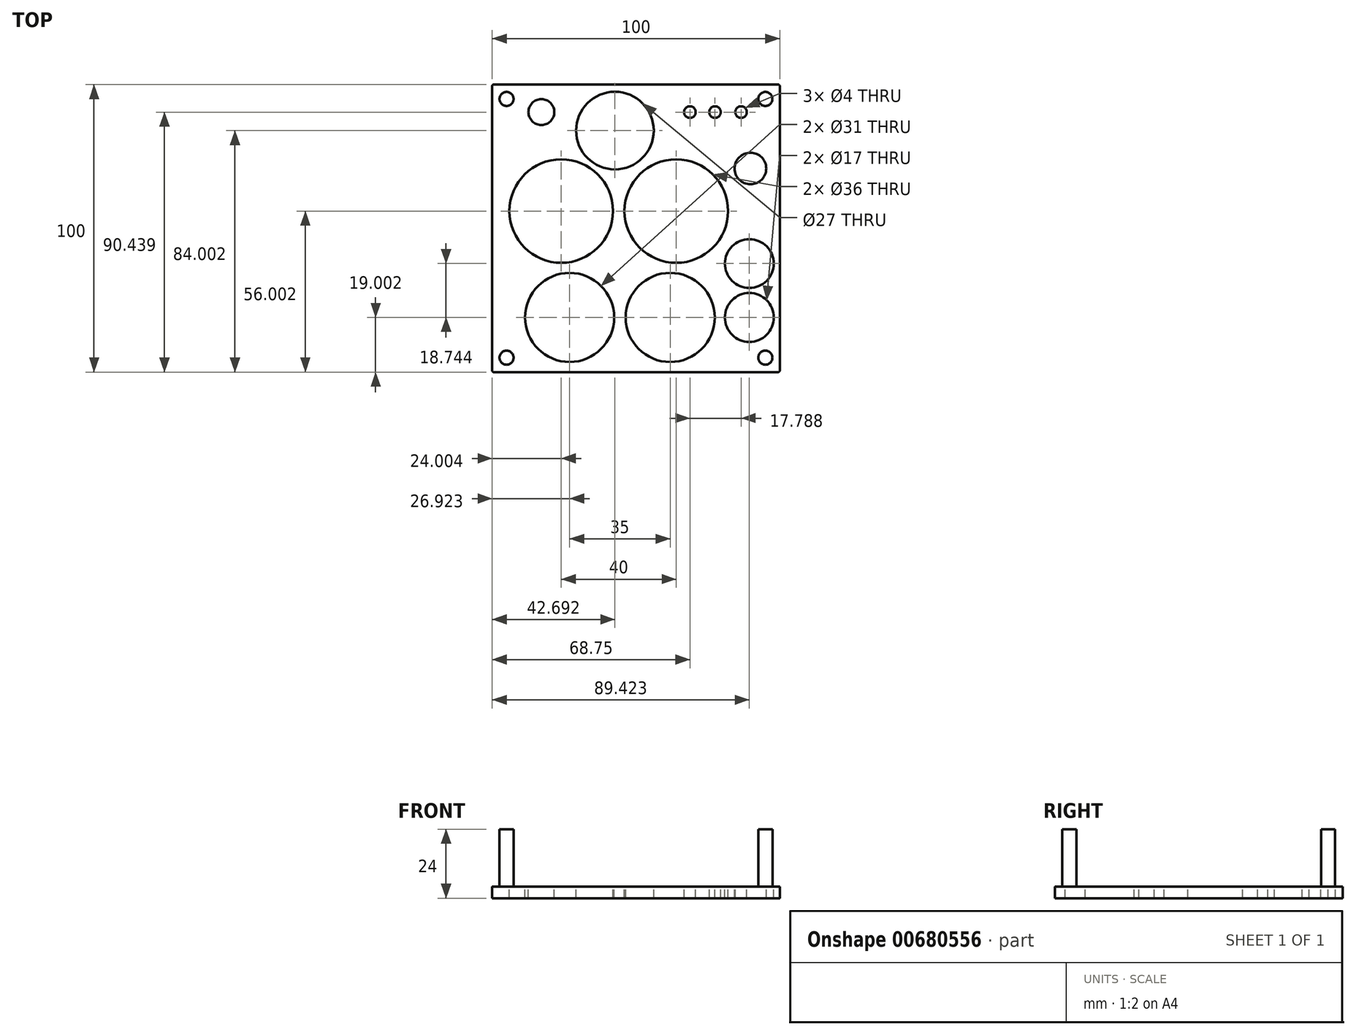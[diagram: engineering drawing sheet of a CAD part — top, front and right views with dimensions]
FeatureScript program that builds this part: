
annotation { "Feature Type Name" : "Feature", "Feature Type Description" : "" }
export const myFeature = defineFeature(function(context is Context, id is Id, definition is map)
    precondition{}
    {
        {
            var Q0;
            Q0=qCreatedBy(makeId("Top.planeOp"),FACE);
            var sketch = newSketch(context, id + "F0", { "sketchPlane" : qUnion([Q0])});
            skLineSegment(sketch, "E0.bottom", {"start": v(-68.75, 48.6) * mm, "end": v(31.25, 48.6) * mm});
            skLineSegment(sketch, "E0.top", {"start": v(-68.75, -51.4) * mm, "end": v(31.25, -51.4) * mm});
            skLineSegment(sketch, "E0.left", {"start": v(-68.75, 48.6) * mm, "end": v(-68.75, -51.4) * mm});
            skLineSegment(sketch, "E0.right", {"start": v(31.25, 48.6) * mm, "end": v(31.25, -51.4) * mm});
            skSolve(sketch);
        }
        {
            var Q0;
            Q0=makeQuery(id+"F0.imprint","IMPRINT",FACE,{"disambiguationData":[TD([[makeQuery(id+"F0.imprint","IMPRINT",EDGE,{"derivedFrom":sQuery(id+"F0.wireOp",EDGE,"E0.bottom")}),-1.0]])]});
            extrude(context, id + "F1", {"entities" : qUnion([Q0]), "depth" : 4 * mm, "offsetDistance" : 25 * mm});
        }
        {
            var Q0;
            Q0=makeQuery(id+"F1.opExtrude","SWEPT_EDGE",EDGE,{"disambiguationData":[OSD([sQuery(id+"F0.wireOp",EDGE,"E0.bottom"),sQuery(id+"F0.wireOp",EDGE,"E0.left")])]});
            var Q1;
            Q1=makeQuery(id+"F1.opExtrude","SWEPT_EDGE",EDGE,{"disambiguationData":[OSD([sQuery(id+"F0.wireOp",EDGE,"E0.bottom"),sQuery(id+"F0.wireOp",EDGE,"E0.right")])]});
            var Q2;
            Q2=makeQuery(id+"F1.opExtrude","SWEPT_EDGE",EDGE,{"disambiguationData":[OSD([sQuery(id+"F0.wireOp",EDGE,"E0.top"),sQuery(id+"F0.wireOp",EDGE,"E0.right")])]});
            var Q3;
            Q3=makeQuery(id+"F1.opExtrude","SWEPT_EDGE",EDGE,{"disambiguationData":[OSD([sQuery(id+"F0.wireOp",EDGE,"E0.top"),sQuery(id+"F0.wireOp",EDGE,"E0.left")])]});
            fillet(context, id + "F2", {"entities" : qUnion([Q0, Q1, Q2, Q3]), "radius" : 0.5 * mm, "tangentPropagation" : true, "allowEdgeOverflow" : false});
        }
        {
            var Q0;
            Q0=makeQuery(id+"F1.opExtrude","CAP_FACE",FACE,{"disambiguationData":[OSD([sQuery(id+"F0.wireOp",EDGE,"E0.bottom"),sQuery(id+"F0.wireOp",EDGE,"E0.top"),sQuery(id+"F0.wireOp",EDGE,"E0.left"),sQuery(id+"F0.wireOp",EDGE,"E0.right")])],"isStart":false});
            var sketch = newSketch(context, id + "F3", { "sketchPlane" : qUnion([Q0])});
            skCircle(sketch, "E1", {"center": v(-63.75, 43.6) * mm, "radius": 2.45 * mm});
            skCircle(sketch, "E2", {"center": v(26.25, 43.6) * mm, "radius": 2.45 * mm});
            skCircle(sketch, "E3", {"center": v(-63.75, -46.4) * mm, "radius": 2.45 * mm});
            skCircle(sketch, "E4", {"center": v(26.25, -46.4) * mm, "radius": 2.45 * mm});
            skSolve(sketch);
        }
        {
            var Q0;
            Q0 = qSketchRegion(id + "F3", true);
            extrude(context, id + "F4", {"entities" : qUnion([Q0]), "operationType" : NewBodyOperationType.ADD, "depth" : 20 * mm, "offsetDistance" : 25 * mm});
        }
        {
            var Q0;
            Q0=makeQuery(id+"F1.opExtrude","CAP_FACE",FACE,{"disambiguationData":[OSD([sQuery(id+"F0.wireOp",EDGE,"E0.bottom"),sQuery(id+"F0.wireOp",EDGE,"E0.top"),sQuery(id+"F0.wireOp",EDGE,"E0.left"),sQuery(id+"F0.wireOp",EDGE,"E0.right")])],"isStart":false});
            var sketch = newSketch(context, id + "F5", { "sketchPlane" : qUnion([Q0])});
            skCircle(sketch, "E5", {"center": v(-44.75, 4.6) * mm, "radius": 18 * mm});
            skCircle(sketch, "E6", {"center": v(-4.75, 4.6) * mm, "radius": 18 * mm});
            skCircle(sketch, "E7", {"center": v(-41.83, -32.4) * mm, "radius": 15.5 * mm});
            skCircle(sketch, "E8", {"center": v(-6.83, -32.4) * mm, "radius": 15.5 * mm});
            skCircle(sketch, "E9", {"center": v(-26.06, 32.6) * mm, "radius": 13.5 * mm});
            skCircle(sketch, "E10", {"center": v(20.67, -32.4) * mm, "radius": 8.5 * mm});
            skCircle(sketch, "E11", {"center": v(20.67, -13.65) * mm, "radius": 8.5 * mm});
            skCircle(sketch, "E12", {"center": v(21.06, 19.42) * mm, "radius": 5.5 * mm});
            skCircle(sketch, "E13", {"center": v(-51.63, 39.04) * mm, "radius": 4.5 * mm});
            skCircle(sketch, "E14", {"center": v(0, 39.04) * mm, "radius": 2 * mm});
            skCircle(sketch, "E15", {"center": v(8.75, 39.04) * mm, "radius": 2 * mm});
            skCircle(sketch, "E16", {"center": v(17.79, 39.04) * mm, "radius": 2 * mm});
            skSolve(sketch);
        }
        {
            var Q0;
            Q0=makeQuery(id+"F5.imprint","IMPRINT",FACE,{"disambiguationData":[TD([[makeQuery(id+"F5.imprint","IMPRINT",EDGE,{"derivedFrom":sQuery(id+"F5.wireOp",EDGE,"E13")}),1.0]])]});
            var Q1;
            Q1=makeQuery(id+"F5.imprint","IMPRINT",FACE,{"disambiguationData":[TD([[makeQuery(id+"F5.imprint","IMPRINT",EDGE,{"derivedFrom":sQuery(id+"F5.wireOp",EDGE,"E9")}),1.0]])]});
            var Q2;
            Q2=makeQuery(id+"F5.imprint","IMPRINT",FACE,{"disambiguationData":[TD([[makeQuery(id+"F5.imprint","IMPRINT",EDGE,{"derivedFrom":sQuery(id+"F5.wireOp",EDGE,"E14")}),1.0]])]});
            var Q3;
            Q3=makeQuery(id+"F5.imprint","IMPRINT",FACE,{"disambiguationData":[TD([[makeQuery(id+"F5.imprint","IMPRINT",EDGE,{"derivedFrom":sQuery(id+"F5.wireOp",EDGE,"E15")}),1.0]])]});
            var Q4;
            Q4=makeQuery(id+"F5.imprint","IMPRINT",FACE,{"disambiguationData":[TD([[makeQuery(id+"F5.imprint","IMPRINT",EDGE,{"derivedFrom":sQuery(id+"F5.wireOp",EDGE,"E16")}),1.0]])]});
            var Q5;
            Q5=makeQuery(id+"F5.imprint","IMPRINT",FACE,{"disambiguationData":[TD([[makeQuery(id+"F5.imprint","IMPRINT",EDGE,{"derivedFrom":sQuery(id+"F5.wireOp",EDGE,"E12")}),1.0]])]});
            var Q6;
            Q6=makeQuery(id+"F5.imprint","IMPRINT",FACE,{"disambiguationData":[TD([[makeQuery(id+"F5.imprint","IMPRINT",EDGE,{"derivedFrom":sQuery(id+"F5.wireOp",EDGE,"E6")}),1.0]])]});
            var Q7;
            Q7=makeQuery(id+"F5.imprint","IMPRINT",FACE,{"disambiguationData":[TD([[makeQuery(id+"F5.imprint","IMPRINT",EDGE,{"derivedFrom":sQuery(id+"F5.wireOp",EDGE,"E5")}),1.0]])]});
            var Q8;
            Q8=makeQuery(id+"F5.imprint","IMPRINT",FACE,{"disambiguationData":[TD([[makeQuery(id+"F5.imprint","IMPRINT",EDGE,{"derivedFrom":sQuery(id+"F5.wireOp",EDGE,"E7")}),1.0]])]});
            var Q9;
            Q9=makeQuery(id+"F5.imprint","IMPRINT",FACE,{"disambiguationData":[TD([[makeQuery(id+"F5.imprint","IMPRINT",EDGE,{"derivedFrom":sQuery(id+"F5.wireOp",EDGE,"E8")}),1.0]])]});
            var Q10;
            Q10=makeQuery(id+"F5.imprint","IMPRINT",FACE,{"disambiguationData":[TD([[makeQuery(id+"F5.imprint","IMPRINT",EDGE,{"derivedFrom":sQuery(id+"F5.wireOp",EDGE,"E11")}),1.0]])]});
            var Q11;
            Q11=makeQuery(id+"F5.imprint","IMPRINT",FACE,{"disambiguationData":[TD([[makeQuery(id+"F5.imprint","IMPRINT",EDGE,{"derivedFrom":sQuery(id+"F5.wireOp",EDGE,"E10")}),1.0]])]});
            extrude(context, id + "F6", {"entities" : qUnion([Q0, Q1, Q2, Q3, Q4, Q5, Q6, Q7, Q8, Q9, Q10, Q11]), "operationType" : NewBodyOperationType.REMOVE, "oppositeDirection" : true, "depth" : 25 * mm, "offsetDistance" : 25 * mm});
        }
    });
